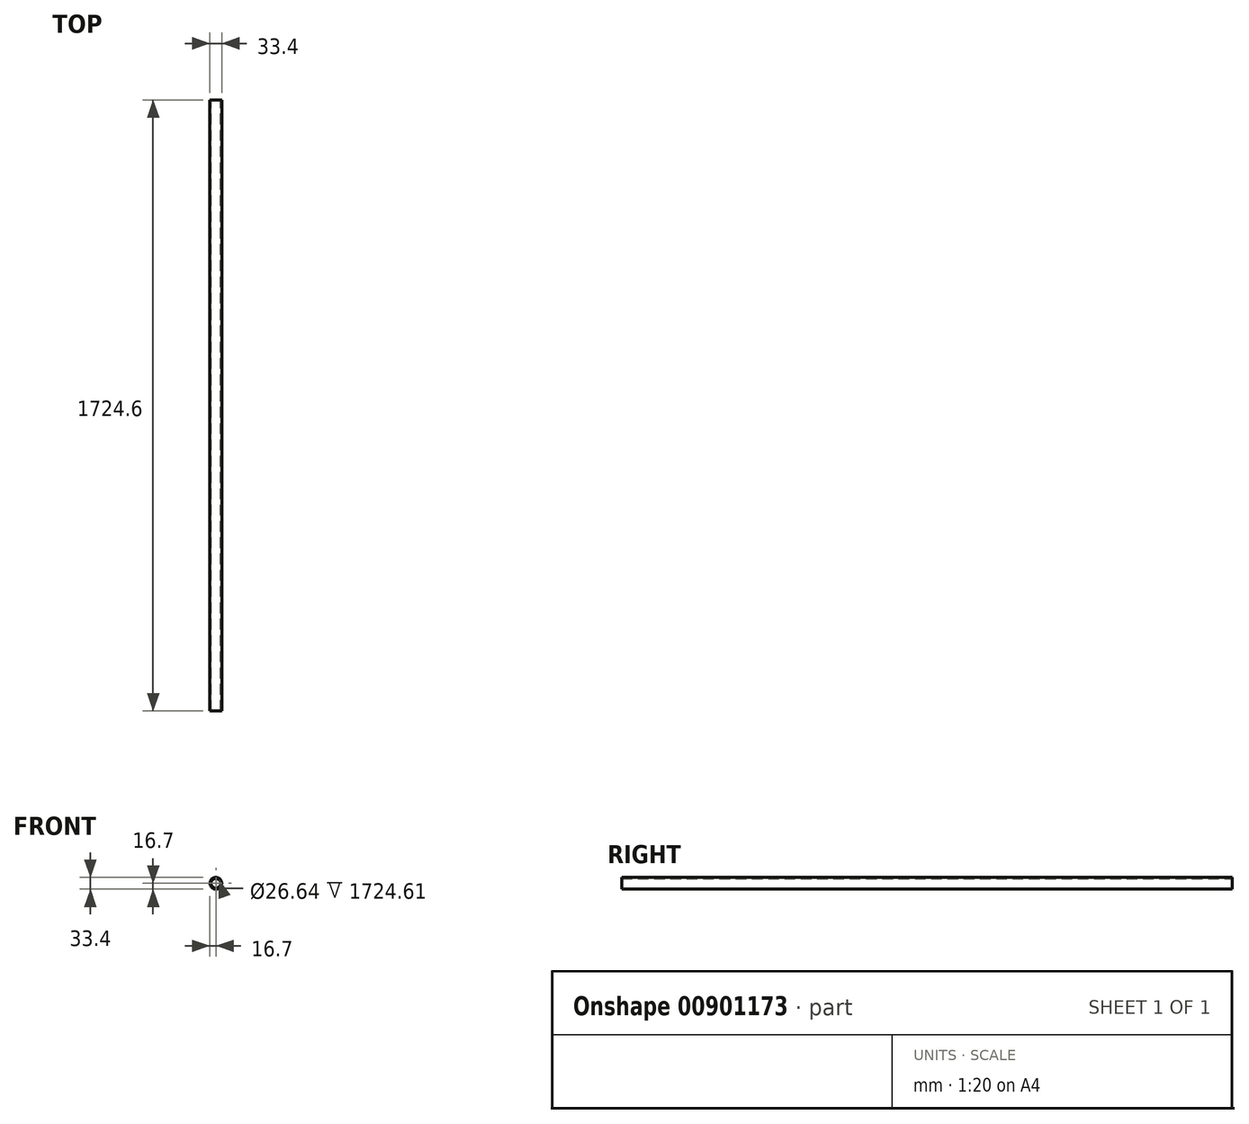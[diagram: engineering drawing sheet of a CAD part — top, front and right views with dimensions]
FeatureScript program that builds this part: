
annotation { "Feature Type Name" : "Feature", "Feature Type Description" : "" }
export const myFeature = defineFeature(function(context is Context, id is Id, definition is map)
    precondition{}
    {
        {
            var Q0;
            Q0=qCreatedBy(makeId("Front.planeOp"),FACE);
            var sketch = newSketch(context, id + "F0", { "sketchPlane" : qUnion([Q0])});
            skCircle(sketch, "E0", {"center": v(0, 0) * mm, "radius": 16.7 * mm});
            skCircle(sketch, "E1", {"center": v(0, 0) * mm, "radius": 13.32 * mm});
            skSolve(sketch);
        }
        {
            var Q0;
            Q0=makeQuery(id+"F0.imprint","IMPRINT",FACE,{"disambiguationData":[TD([[makeQuery(id+"F0.imprint","IMPRINT",EDGE,{"derivedFrom":sQuery(id+"F0.wireOp",EDGE,"E0")}),1.0]])]});
            extrude(context, id + "F1", {"entities" : qUnion([Q0]), "endBound" : BoundingType.SYMMETRIC, "depth" : 1724.6 * mm, "offsetDistance" : 25.4 * mm});
        }
    });
